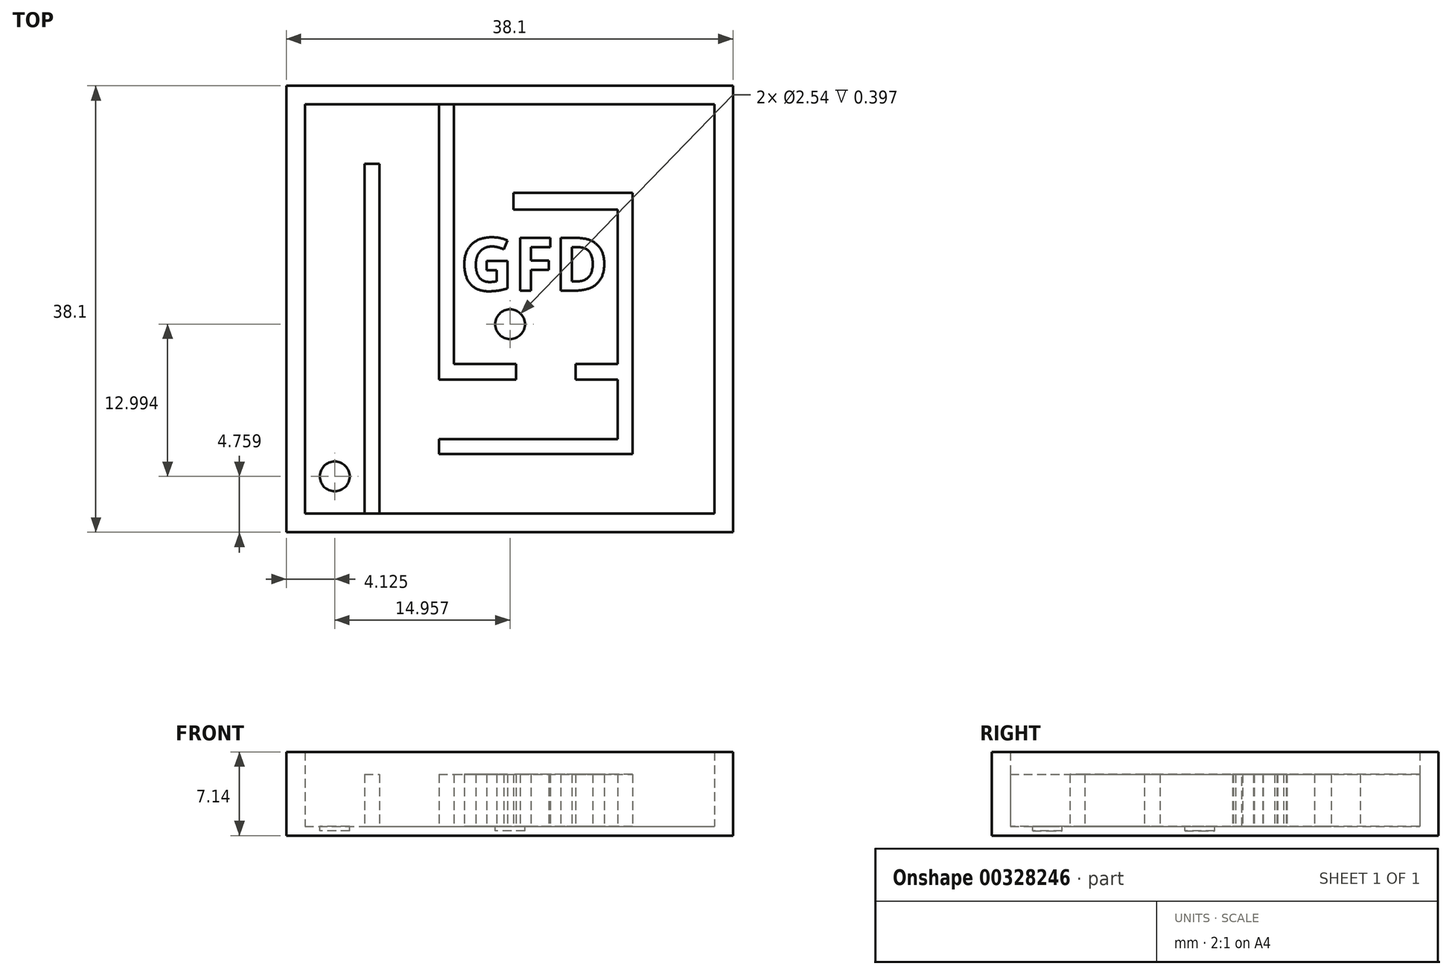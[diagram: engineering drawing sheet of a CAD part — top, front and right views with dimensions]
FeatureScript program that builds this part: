
annotation { "Feature Type Name" : "Feature", "Feature Type Description" : "" }
export const myFeature = defineFeature(function(context is Context, id is Id, definition is map)
    precondition{}
    {
        {
            var Q0;
            Q0=qCreatedBy(makeId("Top.planeOp"),FACE);
            var sketch = newSketch(context, id + "F0", { "sketchPlane" : qUnion([Q0])});
            skLineSegment(sketch, "E0.bottom", {"start": v(-10.92, 5.97) * mm, "end": v(27.18, 5.97) * mm});
            skLineSegment(sketch, "E0.top", {"start": v(-10.92, -32.13) * mm, "end": v(27.18, -32.13) * mm});
            skLineSegment(sketch, "E0.left", {"start": v(-10.92, 5.97) * mm, "end": v(-10.92, -32.13) * mm});
            skLineSegment(sketch, "E0.right", {"start": v(27.18, 5.97) * mm, "end": v(27.18, -32.13) * mm});
            skSolve(sketch);
        }
        {
            var Q0;
            Q0=makeQuery(id+"F0.imprint","IMPRINT",FACE,{"disambiguationData":[TD([[makeQuery(id+"F0.imprint","IMPRINT",EDGE,{"derivedFrom":sQuery(id+"F0.wireOp",EDGE,"E0.bottom")}),-1.0]])]});
            extrude(context, id + "F1", {"entities" : qUnion([Q0]), "depth" : 0.8 * mm});
        }
        {
            var Q0;
            Q0=makeQuery(id+"F1.opExtrude","CAP_FACE",FACE,{"disambiguationData":[OSD([sQuery(id+"F0.wireOp",EDGE,"E0.bottom"),sQuery(id+"F0.wireOp",EDGE,"E0.top"),sQuery(id+"F0.wireOp",EDGE,"E0.left"),sQuery(id+"F0.wireOp",EDGE,"E0.right")])],"isStart":false});
            var sketch = newSketch(context, id + "F2", { "sketchPlane" : qUnion([Q0])});
            skLineSegment(sketch, "E1.0", {"start": v(-9.34, 4.38) * mm, "end": v(25.59, 4.38) * mm});
            skLineSegment(sketch, "E1.1", {"start": v(-9.34, 4.38) * mm, "end": v(-9.34, -30.54) * mm});
            skLineSegment(sketch, "E1.2", {"start": v(-9.34, -30.54) * mm, "end": v(25.59, -30.54) * mm});
            skLineSegment(sketch, "E1.3", {"start": v(25.59, 4.38) * mm, "end": v(25.59, -30.54) * mm});
            skSolve(sketch);
        }
        {
            var Q0;
            Q0=makeQuery(id+"F2.imprint","IMPRINT",FACE,{"disambiguationData":[TD([[makeQuery(id+"F2.imprint","IMPRINT",EDGE,{"derivedFrom":sQuery(id+"F2.wireOp",EDGE,"E1.0")}),1.0]])]});
            extrude(context, id + "F3", {"entities" : qUnion([Q0]), "operationType" : NewBodyOperationType.ADD, "depth" : 6.35 * mm});
        }
        {
            var Q0;
            Q0=makeQuery(id+"F1.opExtrude","CAP_FACE",FACE,{"disambiguationData":[OSD([sQuery(id+"F0.wireOp",EDGE,"E0.bottom"),sQuery(id+"F0.wireOp",EDGE,"E0.top"),sQuery(id+"F0.wireOp",EDGE,"E0.left"),sQuery(id+"F0.wireOp",EDGE,"E0.right")])],"isStart":false});
            var sketch = newSketch(context, id + "F4", { "sketchPlane" : qUnion([Q0])});
            skLineSegment(sketch, "E2.bottom", {"start": v(-4.26, -30.54) * mm, "end": v(-2.99, -30.54) * mm});
            skLineSegment(sketch, "E2.top", {"start": v(-4.26, -0.7) * mm, "end": v(-2.99, -0.7) * mm});
            skLineSegment(sketch, "E2.left", {"start": v(-4.26, -30.54) * mm, "end": v(-4.26, -0.7) * mm});
            skLineSegment(sketch, "E2.right", {"start": v(-2.99, -30.54) * mm, "end": v(-2.99, -0.7) * mm});
            skLineSegment(sketch, "E3", {"start": v(2.1, 4.38) * mm, "end": v(2.1, -19.1) * mm});
            skLineSegment(sketch, "E4", {"start": v(2.1, -25.46) * mm, "end": v(3.36, -25.46) * mm});
            skLineSegment(sketch, "E5", {"start": v(3.36, 4.38) * mm, "end": v(2.1, 4.38) * mm});
            skCircle(sketch, "E6", {"center": v(8.16, -14.38) * mm, "radius": 1.27 * mm});
            skPoint(sketch, "E6.centerSnap0", {"position": v(8.16, -27.8) * mm});
            skCircle(sketch, "E7", {"center": v(-6.8, -27.37) * mm, "radius": 1.27 * mm});
            skPoint(sketch, "E7.centerSnap0", {"position": v(-6.8, -30.54) * mm});
            skPoint(sketch, "E8.orphan", {"position": v(-9.34, -30.54) * mm});
            skPoint(sketch, "E9.start.orphan", {"position": v(4.07, -27.8) * mm});
            skLineSegment(sketch, "E10.bottom", {"start": v(3.36, -25.46) * mm, "end": v(18.6, -25.46) * mm});
            skLineSegment(sketch, "E10.top", {"start": v(3.36, -24.2) * mm, "end": v(17.33, -24.2) * mm});
            skLineSegment(sketch, "E10.right", {"start": v(18.6, -25.46) * mm, "end": v(18.6, -24.2) * mm});
            skLineSegment(sketch, "E11.top", {"start": v(18.6, -3.16) * mm, "end": v(17.33, -3.16) * mm});
            skLineSegment(sketch, "E11.left", {"start": v(18.6, -24.2) * mm, "end": v(18.6, -3.16) * mm});
            skLineSegment(sketch, "E11.right", {"start": v(17.33, -24.2) * mm, "end": v(17.33, -22.35) * mm});
            skLineSegment(sketch, "E12.bottom", {"start": v(17.33, -3.16) * mm, "end": v(8.44, -3.16) * mm});
            skLineSegment(sketch, "E12.top", {"start": v(17.33, -4.6) * mm, "end": v(8.44, -4.6) * mm});
            skLineSegment(sketch, "E12.right", {"start": v(8.44, -3.16) * mm, "end": v(8.44, -4.6) * mm});
            skPoint(sketch, "E13.end.orphan", {"position": v(12.25, -27.8) * mm});
            skLineSegment(sketch, "E14.trimOffspring", {"start": v(3.36, -17.76) * mm, "end": v(3.36, 4.38) * mm});
            skLineSegment(sketch, "E15.trimOffspring", {"start": v(17.33, -17.76) * mm, "end": v(17.33, -4.6) * mm});
            skLineSegment(sketch, "E16", {"start": v(2.1, -19.1) * mm, "end": v(3.36, -19.11) * mm});
            skLineSegment(sketch, "E17", {"start": v(17.33, -19.11) * mm, "end": v(17.33, -22.35) * mm});
            skLineSegment(sketch, "E18.bottom", {"start": v(3.36, -19.11) * mm, "end": v(8.68, -19.11) * mm});
            skLineSegment(sketch, "E18.top", {"start": v(3.36, -17.76) * mm, "end": v(8.68, -17.76) * mm});
            skPoint(sketch, "E19.oppositeSnap0", {"position": v(-2.99, -15.62) * mm});
            skPoint(sketch, "E20.orphan", {"position": v(4.54, -15.62) * mm});
            skLineSegment(sketch, "E21.left", {"start": v(8.68, -17.76) * mm, "end": v(8.68, -19.11) * mm});
            skLineSegment(sketch, "E21.right", {"start": v(13.76, -17.76) * mm, "end": v(13.76, -19.11) * mm});
            skLineSegment(sketch, "E22.trimOffspring", {"start": v(13.76, -17.76) * mm, "end": v(17.33, -17.76) * mm});
            skLineSegment(sketch, "E23.trimOffspring", {"start": v(13.76, -19.11) * mm, "end": v(17.33, -19.11) * mm});
            skLineSegment(sketch, "E24", {"start": v(3.36, -24.2) * mm, "end": v(2.1, -24.2) * mm});
            skLineSegment(sketch, "E25", {"start": v(2.1, -24.2) * mm, "end": v(2.1, -25.46) * mm});
            skSolve(sketch);
        }
        {
            var Q0;
            Q0=makeQuery(id+"F4.imprint","IMPRINT",FACE,{"disambiguationData":[TD([[makeQuery(id+"F4.imprint","IMPRINT",EDGE,{"derivedFrom":sQuery(id+"F4.wireOp",EDGE,"E2.bottom")}),1.0]])]});
            var Q1;
            Q1=makeQuery(id+"F4.imprint","IMPRINT",FACE,{"disambiguationData":[TD([[makeQuery(id+"F4.imprint","IMPRINT",EDGE,{"derivedFrom":sQuery(id+"F4.wireOp",EDGE,"E3")}),1.0]])]});
            extrude(context, id + "F5", {"entities" : qUnion([Q0, Q1]), "operationType" : NewBodyOperationType.ADD, "depth" : 4.44 * mm});
        }
        {
            var Q0;
            Q0=makeQuery(id+"F4.imprint","IMPRINT",FACE,{"disambiguationData":[TD([[makeQuery(id+"F4.imprint","IMPRINT",EDGE,{"derivedFrom":sQuery(id+"F4.wireOp",EDGE,"E6")}),1.0]])]});
            var Q1;
            Q1=makeQuery(id+"F4.imprint","IMPRINT",FACE,{"disambiguationData":[TD([[makeQuery(id+"F4.imprint","IMPRINT",EDGE,{"derivedFrom":sQuery(id+"F4.wireOp",EDGE,"E7")}),1.0]])]});
            extrude(context, id + "F6", {"entities" : qUnion([Q0, Q1]), "operationType" : NewBodyOperationType.REMOVE, "oppositeDirection" : true, "depth" : 0.4 * mm});
        }
        {
            var Q0;
            Q0=makeQuery(id+"F1.opExtrude","CAP_FACE",FACE,{"disambiguationData":[OSD([sQuery(id+"F0.wireOp",EDGE,"E0.bottom"),sQuery(id+"F0.wireOp",EDGE,"E0.top"),sQuery(id+"F0.wireOp",EDGE,"E0.left"),sQuery(id+"F0.wireOp",EDGE,"E0.right")])],"isStart":false});
            var sketch = newSketch(context, id + "F7", { "sketchPlane" : qUnion([Q0])});
            skText(sketch, "E26", { "text": "GFD", "fontName": "OpenSans-Bold.ttf"});
            const initialGuessF7  = {"E26": [0.0039, -0.01151, 1, 0, 0.00453]};
            skSetInitialGuess(sketch, initialGuessF7);
            skSolve(sketch);
        }
        {
            var Q0;
            Q0=makeQuery(id+"F4.imprint","IMPRINT",FACE,{"disambiguationData":[TD([[makeQuery(id+"F4.imprint","IMPRINT",EDGE,{"derivedFrom":sQuery(id+"F4.wireOp",EDGE,"E4")}),1.0]])]});
            var Q1;
            Q1 = qSketchRegion(id + "F7", true);
            extrude(context, id + "F8", {"entities" : qUnion([Q0, Q1]), "operationType" : NewBodyOperationType.ADD, "depth" : 4.44 * mm});
        }
    });
